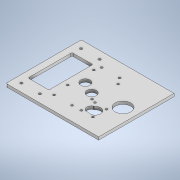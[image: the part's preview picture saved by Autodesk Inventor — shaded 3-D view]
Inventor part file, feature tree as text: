
AUTODESK INVENTOR PART (.ipt)
format: ipt  version: 2021 (Build 250183000, 183)  size: 276,992 bytes
history: native  units: mm
features: sketch x8, extrude x4, hole x4, projected_geometry x2
ambient origin geometry x8: Origin, YZ Plane, XZ Plane, XY Plane, X Axis, Y Axis, Z Axis, Center Point
bodies: Solid1 (feature_tree)
feature tree (18):
  extrude  "Extrusion1"  Depth=76.0mm
  hole  "Hole1"  [1 undecoded]
  hole  "Hole2"  [1 undecoded]
  hole  "Hole3"  [1 undecoded]
  extrude  "Extrusion2"  Depth=4.2mm
  hole  "Hole4"  [1 undecoded]
  extrude  "Extrusion3"  Depth=5.0mm TaperAngle=0.0deg
  extrude  "Extrusion4"  Depth=8.0mm
  sketch  "Sketch1"  dims[d0=36.0mm d1=76.0mm]
  sketch  "Sketch2"  dims[d2=32.0mm d3=103.0mm]
  sketch  "Sketch3"  dims[d4=245.0mm d5=130.0mm]
  sketch  "Sketch4"  dims[d6=11.0mm d7=4.2mm]
  sketch  "Sketch5"  dims[d8=4.2mm d9=4.2mm]
  projected_geometry  "Projected Loop1"
  sketch  "Sketch6"  dims[d10=4.2mm d11=2.0mm]
  sketch  "Sketch7"  dims[d12=2.0mm d13=5.0mm d14=0.0mm]
  sketch  "Sketch9"  dims[d15=31.0mm d16=82.0mm d17=12.0mm d18=3.8mm d19=6.0mm d20=9.4mm d21=2.0mm d22=90.0deg d23=8.0mm d24=20.594885mm d25=90.0mm d26=140.0mm d27=175.0mm d28=27.0mm d29=6.0mm d30=4.0mm d31=2.0mm d32=90.0deg d33=8.0mm d34=20.594885mm d35=23.5mm d36=20.0mm d37=119.5mm d39=3.8mm d40=6.0mm d41=4.0mm d42=2.0mm d43=90.0deg d44=8.0mm d45=20.594885mm d46=82.0mm d47=14.0mm d48=14.0mm d50=3.0mm d52=10.0mm d53=0.0mm d54=36.0mm d55=34.5mm d56=7.5mm d57=7.7mm d58=9.2mm d59=12.7mm d60=42.0mm d61=45.0mm d63=147.0mm d64=3.8mm d65=6.0mm d66=4.0mm d67=2.0mm d68=90.0deg d69=8.0mm d70=20.594885mm d71=34.5mm d72=160.0mm d73=0.0mm d74=0.0mm d75=7.5mm d76=8.0mm d77=11.5mm d78=19.0mm d79=11.8mm d80=16.0mm d81=16.0mm d82=0.0mm d83=0.0mm]
  projected_geometry  "Projected Loop2"
note: 4 required parameter values undecoded (feature->parameter linkage not recoverable at this tier; creation-order binding heuristic only, values carry confidence <= 0.55)
